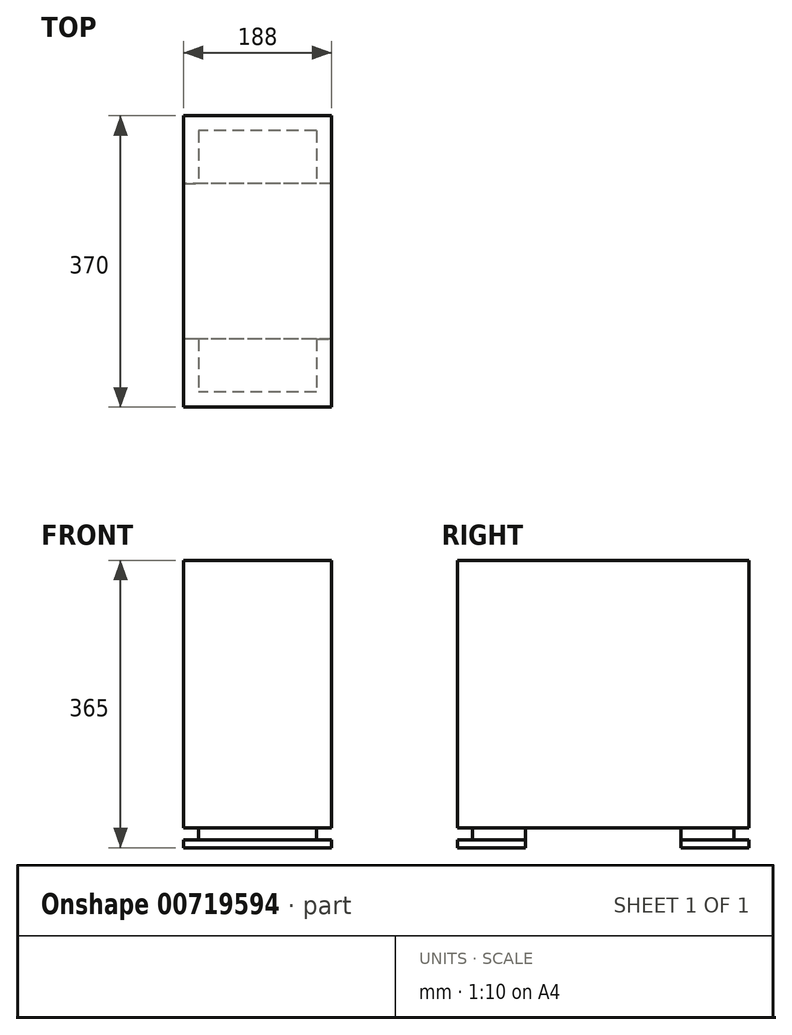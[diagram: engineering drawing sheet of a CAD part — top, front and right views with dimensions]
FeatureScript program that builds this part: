
annotation { "Feature Type Name" : "Feature", "Feature Type Description" : "" }
export const myFeature = defineFeature(function(context is Context, id is Id, definition is map)
    precondition{}
    {
        {
            var Q0;
            Q0=qCreatedBy(makeId("Front.planeOp"),FACE);
            var sketch = newSketch(context, id + "F0", { "sketchPlane" : qUnion([Q0])});
            skLineSegment(sketch, "E0.bottom", {"start": v(0, 0) * mm, "end": v(188, 0) * mm});
            skLineSegment(sketch, "E0.top", {"start": v(0, 365) * mm, "end": v(188, 365) * mm});
            skLineSegment(sketch, "E0.left", {"start": v(0, 0) * mm, "end": v(0, 365) * mm});
            skLineSegment(sketch, "E0.right", {"start": v(188, 0) * mm, "end": v(188, 365) * mm});
            skSolve(sketch);
        }
        {
            var Q0;
            Q0=makeQuery(id+"F0.imprint","IMPRINT",FACE,{"disambiguationData":[TD([[makeQuery(id+"F0.imprint","IMPRINT",EDGE,{"derivedFrom":sQuery(id+"F0.wireOp",EDGE,"E0.bottom")}),1.0]])]});
            extrude(context, id + "F1", {"entities" : qUnion([Q0]), "oppositeDirection" : true, "depth" : 370 * mm, "offsetDistance" : 25 * mm});
        }
        {
            var Q0;
            Q0=makeQuery(id+"F1.opExtrude","SWEPT_FACE",FACE,{"disambiguationData":[OSD([sQuery(id+"F0.wireOp",EDGE,"E0.left")])]});
            var sketch = newSketch(context, id + "F2", { "sketchPlane" : qUnion([Q0])});
            skLineSegment(sketch, "E1", {"start": v(-284, 0) * mm, "end": v(-284, 25) * mm});
            skLineSegment(sketch, "E2", {"start": v(-284, 25) * mm, "end": v(-86, 25) * mm});
            skLineSegment(sketch, "E3", {"start": v(-86, 25) * mm, "end": v(-86, 0) * mm});
            skLineSegment(sketch, "E4", {"start": v(-284, 0) * mm, "end": v(-86, 0) * mm});
            skSolve(sketch);
        }
        {
            var Q0;
            Q0=makeQuery(id+"F2.imprint","IMPRINT",FACE,{"disambiguationData":[TD([[makeQuery(id+"F2.imprint","IMPRINT",EDGE,{"derivedFrom":sQuery(id+"F2.wireOp",EDGE,"E1")}),-1.0]])]});
            extrude(context, id + "F3", {"entities" : qUnion([Q0]), "operationType" : NewBodyOperationType.REMOVE, "endBound" : BoundingType.THROUGH_ALL, "oppositeDirection" : true, "depth" : 25 * mm, "offsetDistance" : 25 * mm});
        }
        {
            var Q0;
            Q0=makeQuery(id+"F1.opExtrude","CAP_FACE",FACE,{"disambiguationData":[OSD([sQuery(id+"F0.wireOp",EDGE,"E0.bottom"),sQuery(id+"F0.wireOp",EDGE,"E0.top"),sQuery(id+"F0.wireOp",EDGE,"E0.left"),sQuery(id+"F0.wireOp",EDGE,"E0.right")])],"isStart":true});
            var sketch = newSketch(context, id + "F4", { "sketchPlane" : qUnion([Q0])});
            skLineSegment(sketch, "E5", {"start": v(0, 10.16) * mm, "end": v(19.05, 10.16) * mm});
            skLineSegment(sketch, "E6", {"start": v(19.05, 10.16) * mm, "end": v(19.05, 25) * mm});
            skLineSegment(sketch, "E7", {"start": v(19.05, 25) * mm, "end": v(0, 25) * mm});
            skLineSegment(sketch, "E8", {"start": v(0, 25) * mm, "end": v(0, 10.16) * mm});
            skLineSegment(sketch, "E9", {"start": v(94, 0) * mm, "end": v(94, 365) * mm, "construction": true});
            skLineSegment(sketch, "E10.MirrorCS", {"start": v(168.95, 25) * mm, "end": v(188, 25) * mm});
            skLineSegment(sketch, "E11.MirrorCS", {"start": v(188, 25) * mm, "end": v(188, 10.16) * mm});
            skLineSegment(sketch, "E12.MirrorCS", {"start": v(188, 10.16) * mm, "end": v(168.95, 10.16) * mm});
            skLineSegment(sketch, "E13.MirrorCS", {"start": v(168.95, 10.16) * mm, "end": v(168.95, 25) * mm});
            skSolve(sketch);
        }
        {
            var Q0;
            Q0 = qSketchRegion(id + "F4", true);
            extrude(context, id + "F5", {"entities" : qUnion([Q0]), "operationType" : NewBodyOperationType.REMOVE, "endBound" : BoundingType.THROUGH_ALL, "oppositeDirection" : true, "depth" : 25.4 * mm, "offsetDistance" : 25.4 * mm});
        }
        {
            var Q0;
            {var subQ0=sQuery(id+"F0.wireOp",EDGE,"E0.top");var subQ2=sQuery(id+"F0.wireOp",EDGE,"E0.left");Q0=makeQuery(id+"F5.boolean.opBoolean","SPLIT",FACE,{"disambiguationData":[TD([makeQuery(id+"F1.opExtrude","SWEPT_FACE",FACE,{"disambiguationData":[OSD([subQ0])]})])],"derivedFrom":makeQuery(id+"F1.opExtrude","SWEPT_FACE",FACE,{"disambiguationData":[OSD([subQ2])]})});}
            var sketch = newSketch(context, id + "F6", { "sketchPlane" : qUnion([Q0])});
            skLineSegment(sketch, "E14.bottom", {"start": v(-370, 25) * mm, "end": v(-350.95, 25) * mm});
            skLineSegment(sketch, "E14.top", {"start": v(-370, 10.16) * mm, "end": v(-350.95, 10.16) * mm});
            skLineSegment(sketch, "E14.left", {"start": v(-370, 25) * mm, "end": v(-370, 10.16) * mm});
            skLineSegment(sketch, "E14.right", {"start": v(-350.95, 25) * mm, "end": v(-350.95, 10.16) * mm});
            skLineSegment(sketch, "E15", {"start": v(-185, 25) * mm, "end": v(-185, 365) * mm, "construction": true});
            skLineSegment(sketch, "E16.MirrorCS", {"start": v(-19.05, 25) * mm, "end": v(-19.05, 10.16) * mm});
            skLineSegment(sketch, "E17.MirrorCS", {"start": v(0, 25) * mm, "end": v(-19.05, 25) * mm});
            skLineSegment(sketch, "E18.MirrorCS", {"start": v(0, 25) * mm, "end": v(0, 10.16) * mm});
            skLineSegment(sketch, "E19.MirrorCS", {"start": v(0, 10.16) * mm, "end": v(-19.05, 10.16) * mm});
            skSolve(sketch);
        }
        {
            var Q0;
            Q0=makeQuery(id+"F6.imprint","IMPRINT",FACE,{"disambiguationData":[TD([[makeQuery(id+"F6.imprint","IMPRINT",EDGE,{"derivedFrom":sQuery(id+"F6.wireOp",EDGE,"E14.bottom")}),-1.0]])]});
            var Q1;
            Q1=makeQuery(id+"F6.imprint","IMPRINT",FACE,{"disambiguationData":[TD([[makeQuery(id+"F6.imprint","IMPRINT",EDGE,{"derivedFrom":sQuery(id+"F6.wireOp",EDGE,"E16.MirrorCS")}),1.0]])]});
            extrude(context, id + "F7", {"entities" : qUnion([Q0, Q1]), "operationType" : NewBodyOperationType.REMOVE, "endBound" : BoundingType.THROUGH_ALL, "oppositeDirection" : true, "depth" : 25.4 * mm, "offsetDistance" : 25.4 * mm});
        }
    });
